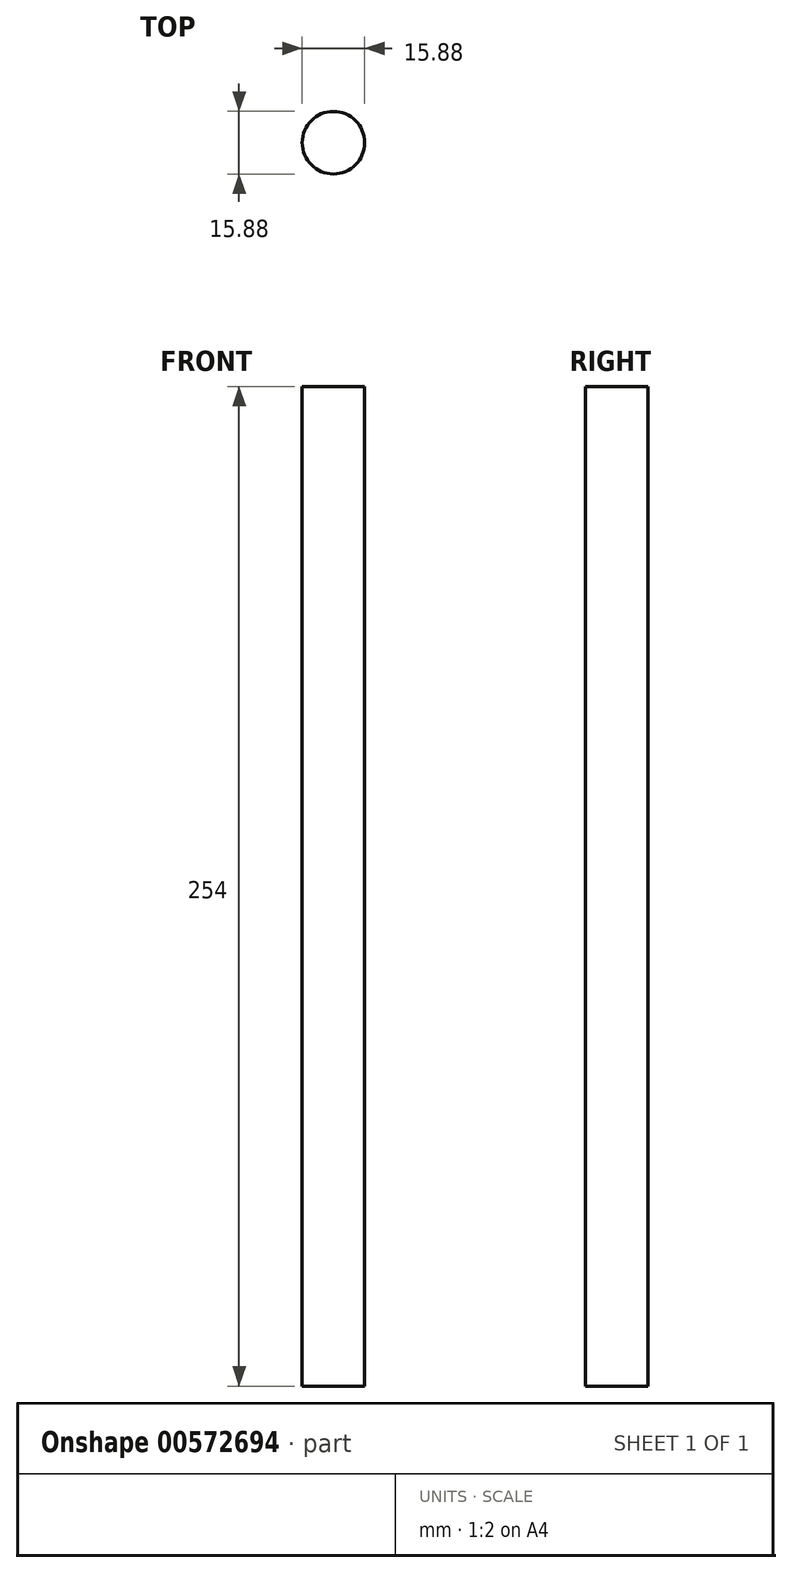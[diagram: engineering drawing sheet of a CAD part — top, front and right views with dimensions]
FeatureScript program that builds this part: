
annotation { "Feature Type Name" : "Feature", "Feature Type Description" : "" }
export const myFeature = defineFeature(function(context is Context, id is Id, definition is map)
    precondition{}
    {
        {
            var Q0;
            Q0=qCreatedBy(makeId("Top.planeOp"),FACE);
            var sketch = newSketch(context, id + "F0", { "sketchPlane" : qUnion([Q0])});
            skCircle(sketch, "E0", {"center": v(0, 0) * mm, "radius": 7.94 * mm});
            skSolve(sketch);
        }
        {
            var Q0;
            Q0 = qSketchRegion(id + "F0", true);
            extrude(context, id + "F1", {"entities" : qUnion([Q0]), "oppositeDirection" : true, "depth" : 254 * mm, "offsetDistance" : 25.4 * mm});
        }
    });
